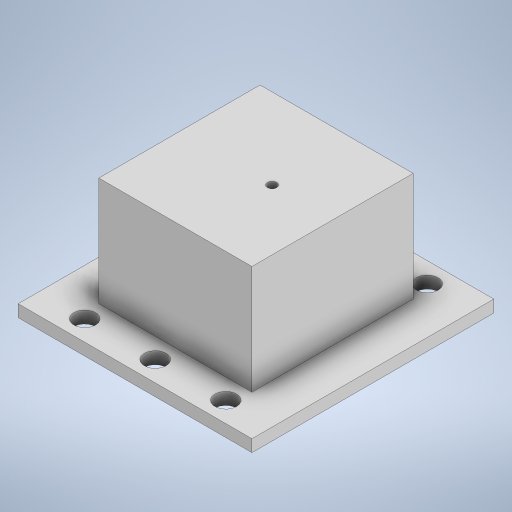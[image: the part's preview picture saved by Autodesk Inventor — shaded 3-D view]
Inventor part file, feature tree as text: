
AUTODESK INVENTOR PART (.ipt)
format: ipt  version: 2024 (Build 280153000, 153)  size: 319,488 bytes
history: native  units: mm
features: extrude x7, sketch x7, plane x3
ambient origin geometry x8: Origin, YZ Plane, XZ Plane, XY Plane, X Axis, Y Axis, Z Axis, Center Point
bodies: Body1 (feature_tree)
feature tree (17):
  plane  "Work Plane5"
  extrude  "Extrusion34"  Depth=40.0mm
  plane  "Work Plane2"
  extrude  "Extrusion35"  Depth=30.0mm
  plane  "Work Plane1"
  extrude  "Extrusion51"  Depth=30.0mm
  sketch  "Sketch77"  dims[d211=10.0mm d212=0.0mm d219=35.0mm]
  extrude  "Extrusion53"  Depth=10.0mm
  extrude  "Extrusion54"  Depth=60.0mm
  extrude  "Extrusion56"  Depth=3.0mm TaperAngle=0.0deg
  extrude  "Extrusion57"  Depth=4.5mm
  sketch  "Sketch45"  dims[d142=38.0mm d143=40.0mm]
  sketch  "Sketch47"  dims[d144=30.0mm d145=0.0mm d146=36.0mm]
  sketch  "Sketch74"  dims[d147=30.0mm d148=-2.617994mm d210=2.3mm]
  sketch  "Sketch78"  dims[d220=58.0mm d221=60.0mm]
  sketch  "Sketch81"  dims[d222=3.0mm d223=0.0mm d224=3.0mm d225=0.0mm]
  sketch  "Sketch83"  dims[d232=5.0mm d233=11.5mm d234=5.4mm d235=17.5mm d236=5.4mm d237=17.5mm d238=5.4mm d239=5.0mm d240=17.0mm d241=5.4mm d242=16.0mm d243=5.4mm d244=17.0mm d245=5.4mm d246=17.5mm d247=5.4mm d248=17.5mm d249=5.0mm d250=30.0mm d251=0.0mm d253=4.0mm d254=4.5mm d255=0.0mm d49=0.5mm d50=0.872665mm d51=0.5mm d52=0.872665mm d130=0.5mm d131=0.872665mm d132=0.5mm d133=0.872665mm d156=0.5mm d157=0.872665mm d158=0.5mm d159=0.872665mm d173=0.5mm d174=0.872665mm d175=0.5mm d176=0.872665mm d226=0.5mm d227=0.872665mm]
